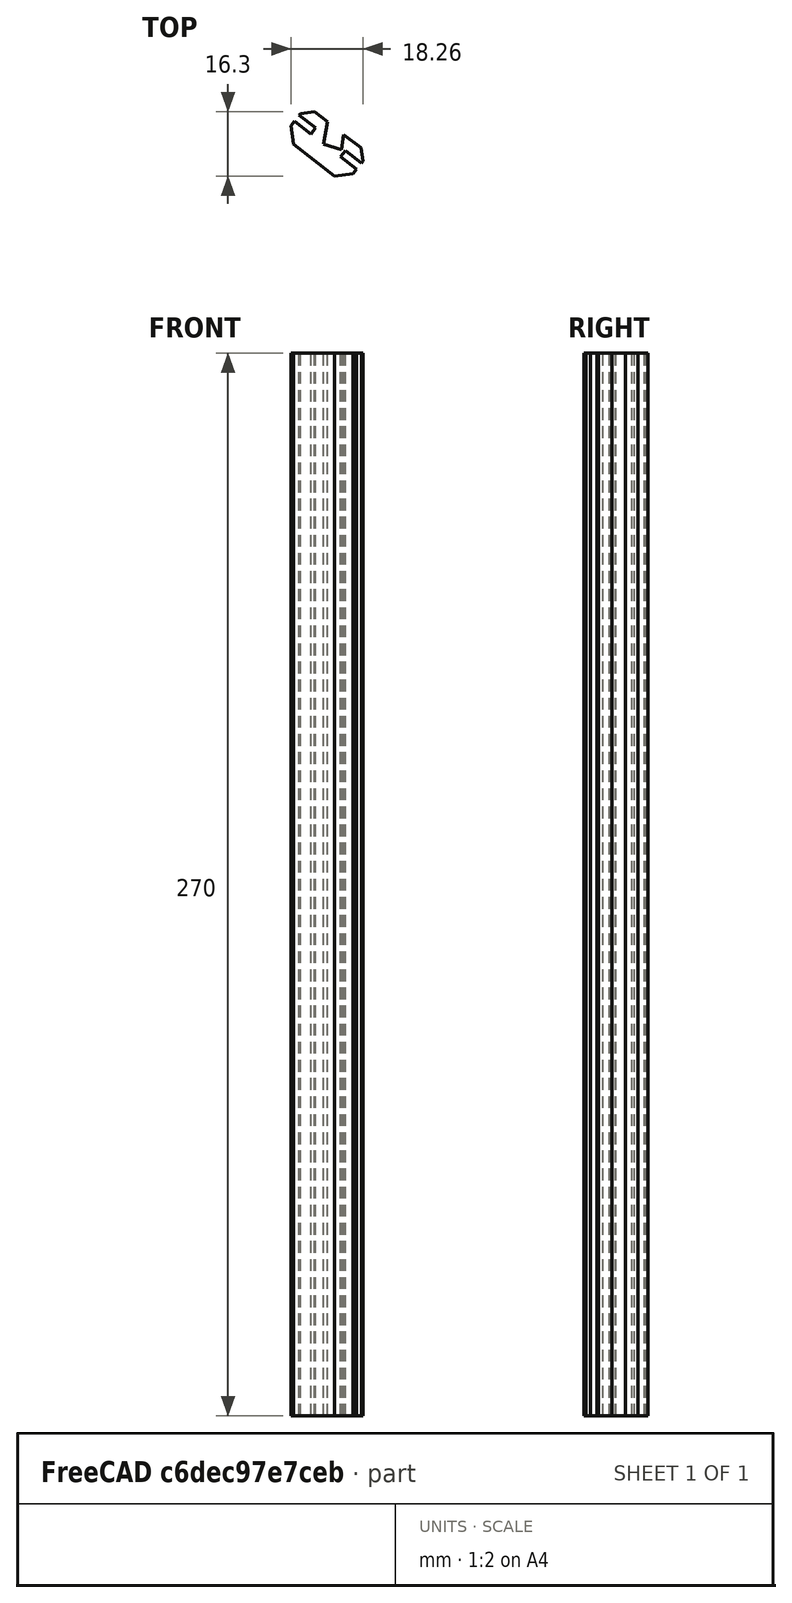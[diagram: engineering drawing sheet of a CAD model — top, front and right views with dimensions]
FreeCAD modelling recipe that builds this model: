
FCSTD DOCUMENT  (FreeCAD 0.21R33771 (Git))
Label: Боковая частьъ
License: All rights reserved
LicenseURL: https://en.wikipedia.org/wiki/All_rights_reserved
objects: Sketcher::SketchObject×1, PartDesign::Pad×1, PartDesign::Body×1
note: 4 computed .brp shape members not serialized (recipe doc carries the construction recipe); baked Part::Feature solids carry a one-line shape summary decoded from their .brp

FEATURE [Sketcher::SketchObject] Sketch
  AttachmentOffset = pos=(0,0,-458) rot=(0,0,1;0rad)
  FullyConstrained = false
  MapMode = 5
  Placement = pos=(0,0,-458) rot=(0,0,1;0rad)
  Support = -> [XY_Plane014]
  sketch-geometry (34):
    g0: LineSegment StartX=-412.208 StartY=1527.42 StartZ=0 EndX=-356.389 EndY=1451.87 EndZ=0
    g1: LineSegment StartX=225.174 StartY=72.7484 StartZ=0 EndX=226.923 EndY=85.8243 EndZ=0
    g2: LineSegment StartX=219.908 StartY=71.1594 StartZ=0 EndX=222.407 EndY=85.6869 EndZ=0
    g3: LineSegment StartX=219.908 StartY=71.1594 StartZ=0 EndX=221.677 EndY=69.9117 EndZ=0
    g4: LineSegment StartX=221.677 StartY=69.9117 StartZ=0 EndX=223.064 EndY=70.1126 EndZ=0
    g5: LineSegment StartX=223.064 StartY=70.1126 StartZ=0 EndX=225.174 EndY=72.7484 EndZ=0
    g6: LineSegment StartX=212.857 StartY=82.9677 StartZ=0 EndX=213.718 EndY=84.0658 EndZ=0
    g7: LineSegment StartX=213.718 StartY=84.0658 StartZ=0 EndX=217.887 EndY=80.7979 EndZ=0
    g8: LineSegment StartX=217.887 StartY=80.7979 StartZ=0 EndX=219.106 EndY=82.4002 EndZ=0
    g9: LineSegment StartX=219.106 StartY=82.4002 StartZ=0 EndX=214.945 EndY=85.5862 EndZ=0
    g10: LineSegment StartX=214.945 StartY=85.5862 StartZ=0 EndX=215.264 EndY=85.9848 EndZ=0
    g11: LineSegment StartX=215.264 StartY=85.9848 StartZ=0 EndX=218.771 EndY=86.4312 EndZ=0
    g12: LineSegment StartX=218.771 StartY=86.4312 StartZ=0 EndX=222.094 EndY=83.8722 EndZ=0
    g13: LineSegment StartX=230.66 StartY=77.3182 StartZ=0 EndX=231.115 EndY=73.836 EndZ=0
    g14: LineSegment StartX=231.115 StartY=73.836 StartZ=0 EndX=230.812 EndY=73.4135 EndZ=0
    g15: LineSegment StartX=230.812 StartY=73.4135 StartZ=0 EndX=226.654 EndY=76.5973 EndZ=0
    g16: LineSegment StartX=226.654 StartY=76.5973 StartZ=0 EndX=225.421 EndY=75.0089 EndZ=0
    g17: LineSegment StartX=225.421 StartY=75.0089 StartZ=0 EndX=229.506 EndY=71.8327 EndZ=0
    g18: LineSegment StartX=229.506 StartY=71.8327 StartZ=0 EndX=228.643 EndY=70.7215 EndZ=0
    g19: LineSegment StartX=223.936 StartY=70.1283 StartZ=0 EndX=213.441 EndY=78.2597 EndZ=0
    g20: LineSegment StartX=222.094 StartY=83.8722 StartZ=0 EndX=221.124 EndY=78.2327 EndZ=0
    g21: LineSegment StartX=226.232 StartY=80.6575 StartZ=0 EndX=225.725 EndY=76.8708 EndZ=0
    g22: LineSegment StartX=221.124 StartY=78.2327 StartZ=0 EndX=225.725 EndY=76.8708 EndZ=0
    g23: LineSegment StartX=226.232 StartY=80.6575 StartZ=0 EndX=230.66 EndY=77.3182 EndZ=0
    g24: LineSegment StartX=212.857 StartY=82.9677 StartZ=0 EndX=213.441 EndY=78.2597 EndZ=0
    g25: LineSegment StartX=223.936 StartY=70.1283 StartZ=0 EndX=228.643 EndY=70.7215 EndZ=0
    g26: LineSegment StartX=225.993 StartY=72.7743 StartZ=0 EndX=223.936 EndY=70.1283 EndZ=0
    g27: LineSegment StartX=223.936 StartY=70.1283 StartZ=0 EndX=226.585 EndY=68.0755 EndZ=0
    g28: LineSegment StartX=226.585 StartY=68.0755 StartZ=0 EndX=228.643 EndY=70.7215 EndZ=0
    g29: LineSegment StartX=228.643 StartY=70.7215 StartZ=0 EndX=225.993 EndY=72.7743 EndZ=0
    g30: LineSegment StartX=212.857 StartY=82.9677 StartZ=0 EndX=210.782 EndY=80.3201 EndZ=0
    g31: LineSegment StartX=210.782 StartY=80.3201 StartZ=0 EndX=213.441 EndY=78.2597 EndZ=0
    g32: LineSegment StartX=213.441 StartY=78.2597 StartZ=0 EndX=215.516 EndY=80.9073 EndZ=0
    g33: LineSegment StartX=215.516 StartY=80.9073 StartZ=0 EndX=212.857 EndY=82.9677 EndZ=0
  constraints (52):
    c: Coincident(g3,g2)
    c: Coincident(g4,g3)
    c: Coincident(g5,g4)
    c: Coincident(g5,g1)
    c: Coincident(g7,g8)
    c: Coincident(g8,g9)
    c: Coincident(g9,g10)
    c: Coincident(g10,g11)
    c: Coincident(g11,g12)
    c: Coincident(g23,g13)
    c: Coincident(g13,g14)
    c: Coincident(g14,g15)
    c: Coincident(g15,g16)
    c: Coincident(g16,g17)
    c: Coincident(g17,g18)
    c: PointOnObject(g20,g2)
    c: PointOnObject(g21,g1)
    c: Coincident(g22,g20)
    c: Coincident(g22,g21)
    c: PointOnObject(g12,g2)
    c: Coincident(g20,g12)
    c: Coincident(g21,g23)
    c: PointOnObject(g21,g1)
    c: Perpendicular(g18,g17)
    c: Block(g17)
    c: Block(g7)
    c: PointOnObject(g24,g6)
    c: PointOnObject(g25,g18)
    c: Equal(g25,g24)
    c: Block(g6)
    c: Coincident(g26,g27)
    c: Coincident(g27,g28)
    c: Coincident(g28,g29)
    c: Coincident(g29,g26)
    c: Equal(g29,g26)
    c: Equal(g26,g27)
    c: Equal(g27,g28)
    c: Coincident(g28,g25)
    c: Coincident(g26,g25)
    c: Coincident(g30,g31)
    c: Coincident(g31,g32)
    c: Coincident(g32,g33)
    c: Coincident(g33,g30)
    c: Equal(g33,g30)
    c: Equal(g30,g32)
    c: Equal(g32,g31)
    c: Coincident(g31,g24)
    c: Coincident(g24,g30)
    c: Coincident(g19,g24)
    c: PointOnObject(g6,g33)
    c: Coincident(g19,g25)
    c: PointOnObject(g18,g29)
FEATURE [PartDesign::Pad] Pad
  Direction = (0,0,1)
  Length = 270
  Length2 = 10
  Profile = -> Sketch
  ReferenceAxis = -> Sketch [N_Axis]
  Type = 0
FEATURE [PartDesign::Body] Body  label="Тело"
  Group = -> [Sketch,Pad]
  Origin = -> Origin014
  Tip = -> Pad
